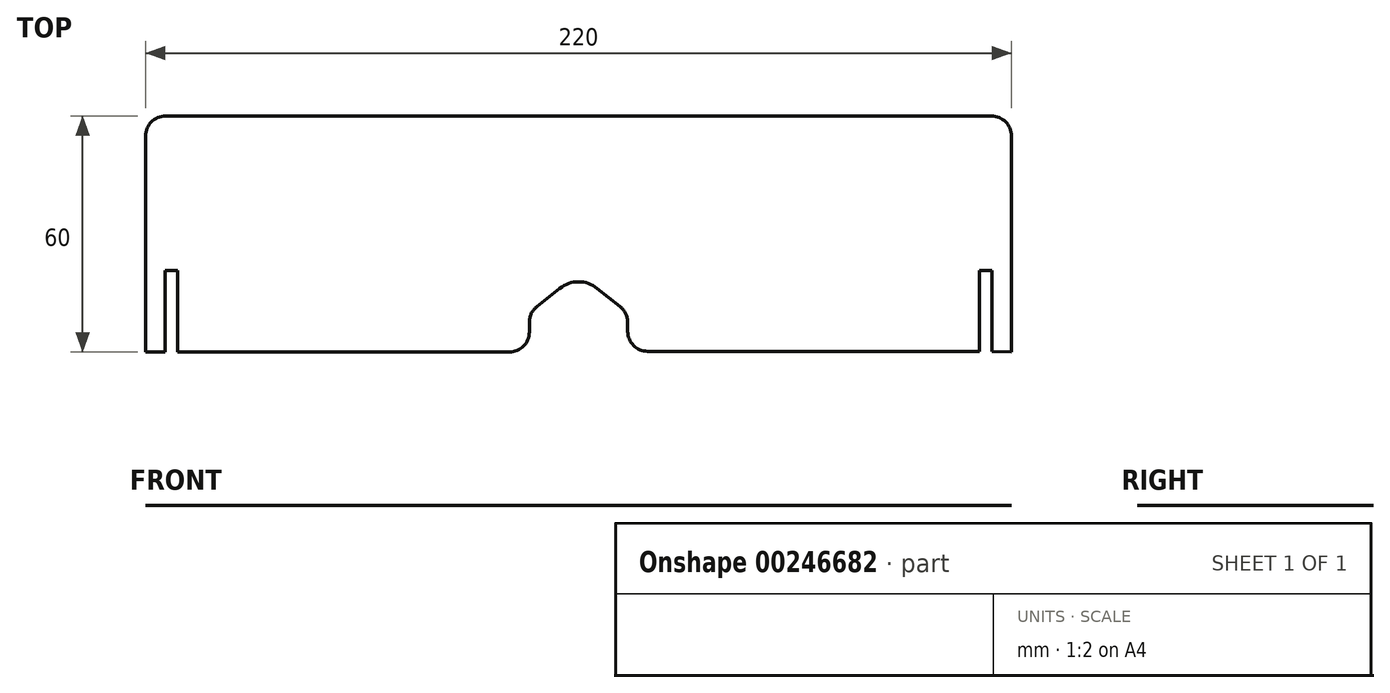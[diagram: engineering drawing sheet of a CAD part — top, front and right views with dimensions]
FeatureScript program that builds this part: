
annotation { "Feature Type Name" : "Feature", "Feature Type Description" : "" }
export const myFeature = defineFeature(function(context is Context, id is Id, definition is map)
    precondition{}
    {
        {
            var Q0;
            Q0=qCreatedBy(makeId("Top.planeOp"),FACE);
            var sketch = newSketch(context, id + "F0", { "sketchPlane" : qUnion([Q0])});
            skLineSegment(sketch, "E0.bottom", {"start": v(104.92, 30) * mm, "end": v(-104.92, 30) * mm});
            skLineSegment(sketch, "E0.left", {"start": v(110, 24.92) * mm, "end": v(110, -30) * mm});
            skLineSegment(sketch, "E0.right", {"start": v(-110, 24.92) * mm, "end": v(-110, -30) * mm});
            skPoint(sketch, "E0.middle", {"position": v(0, 0) * mm});
            skLineSegment(sketch, "E1", {"start": v(-110, -10) * mm, "end": v(110, -10) * mm, "construction": true});
            skLineSegment(sketch, "E2", {"start": v(0, 30) * mm, "end": v(0, -30) * mm, "construction": true});
            skLineSegment(sketch, "E3", {"start": v(-110, -20) * mm, "end": v(110, -20) * mm, "construction": true});
            skLineSegment(sketch, "E4", {"start": v(-12.5, -24.92) * mm, "end": v(-12.5, -22.44) * mm});
            skLineSegment(sketch, "E5", {"start": v(-10.6, -18.47) * mm, "end": v(-4.76, -13.8) * mm});
            skPoint(sketch, "E6.visualSharp", {"position": v(0, -10) * mm});
            skLineSegment(sketch, "E7", {"start": v(12.5, -22.44) * mm, "end": v(12.5, -24.73) * mm});
            skLineSegment(sketch, "E8", {"start": v(4.76, -13.8) * mm, "end": v(10.6, -18.47) * mm});
            skArc(sketch, "E9.filletArc", {"start": v(4.76, -13.8) * mm, "mid": v(0, -12.14) * mm, "end": v(-4.76, -13.8) * mm});
            skLineSegment(sketch, "E10.top", {"start": v(-105, -9.23) * mm, "end": v(-101.83, -9.23) * mm});
            skLineSegment(sketch, "E10.left", {"start": v(-105, -30) * mm, "end": v(-105, -9.23) * mm});
            skLineSegment(sketch, "E10.right", {"start": v(-101.83, -30) * mm, "end": v(-101.83, -9.23) * mm});
            skLineSegment(sketch, "E11.top", {"start": v(105, -9.23) * mm, "end": v(101.83, -9.23) * mm});
            skLineSegment(sketch, "E11.left", {"start": v(105, -29.8) * mm, "end": v(105, -9.23) * mm});
            skLineSegment(sketch, "E11.right", {"start": v(101.83, -29.8) * mm, "end": v(101.83, -9.23) * mm});
            skLineSegment(sketch, "E12", {"start": v(-110, -30) * mm, "end": v(-105, -30) * mm});
            skLineSegment(sketch, "E13", {"start": v(-101.82, -30) * mm, "end": v(-17.58, -30) * mm});
            skLineSegment(sketch, "E14", {"start": v(17.58, -29.8) * mm, "end": v(101.83, -29.8) * mm});
            skLineSegment(sketch, "E15", {"start": v(105, -29.8) * mm, "end": v(110, -30) * mm});
            skPoint(sketch, "E16.visualSharp", {"position": v(-12.5, -20) * mm});
            skArc(sketch, "E16.filletArc", {"start": v(-10.6, -18.47) * mm, "mid": v(-12, -20.24) * mm, "end": v(-12.5, -22.44) * mm});
            skPoint(sketch, "E17.visualSharp", {"position": v(-12.5, -30) * mm});
            skArc(sketch, "E17.filletArc", {"start": v(-17.58, -30) * mm, "mid": v(-13.99, -28.51) * mm, "end": v(-12.5, -24.92) * mm});
            skPoint(sketch, "E18.visualSharp", {"position": v(12.5, -20) * mm});
            skArc(sketch, "E18.filletArc", {"start": v(12.5, -22.44) * mm, "mid": v(12, -20.24) * mm, "end": v(10.6, -18.47) * mm});
            skPoint(sketch, "E19.visualSharp", {"position": v(12.5, -29.8) * mm});
            skArc(sketch, "E19.filletArc", {"start": v(12.5, -24.73) * mm, "mid": v(13.99, -28.32) * mm, "end": v(17.58, -29.8) * mm});
            skPoint(sketch, "E20.visualSharp", {"position": v(-110, 30) * mm});
            skArc(sketch, "E20.filletArc", {"start": v(-104.92, 30) * mm, "mid": v(-108.51, 28.51) * mm, "end": v(-110, 24.92) * mm});
            skPoint(sketch, "E21.visualSharp", {"position": v(110, 30) * mm});
            skArc(sketch, "E21.filletArc", {"start": v(110, 24.92) * mm, "mid": v(108.51, 28.51) * mm, "end": v(104.92, 30) * mm});
            skSolve(sketch);
        }
        {
            var Q0;
            Q0 = qSketchRegion(id + "F0", true);
            extrude(context, id + "F1", {"entities" : qUnion([Q0]), "depth" : 1 / 203.2 * mm});
        }
    });
